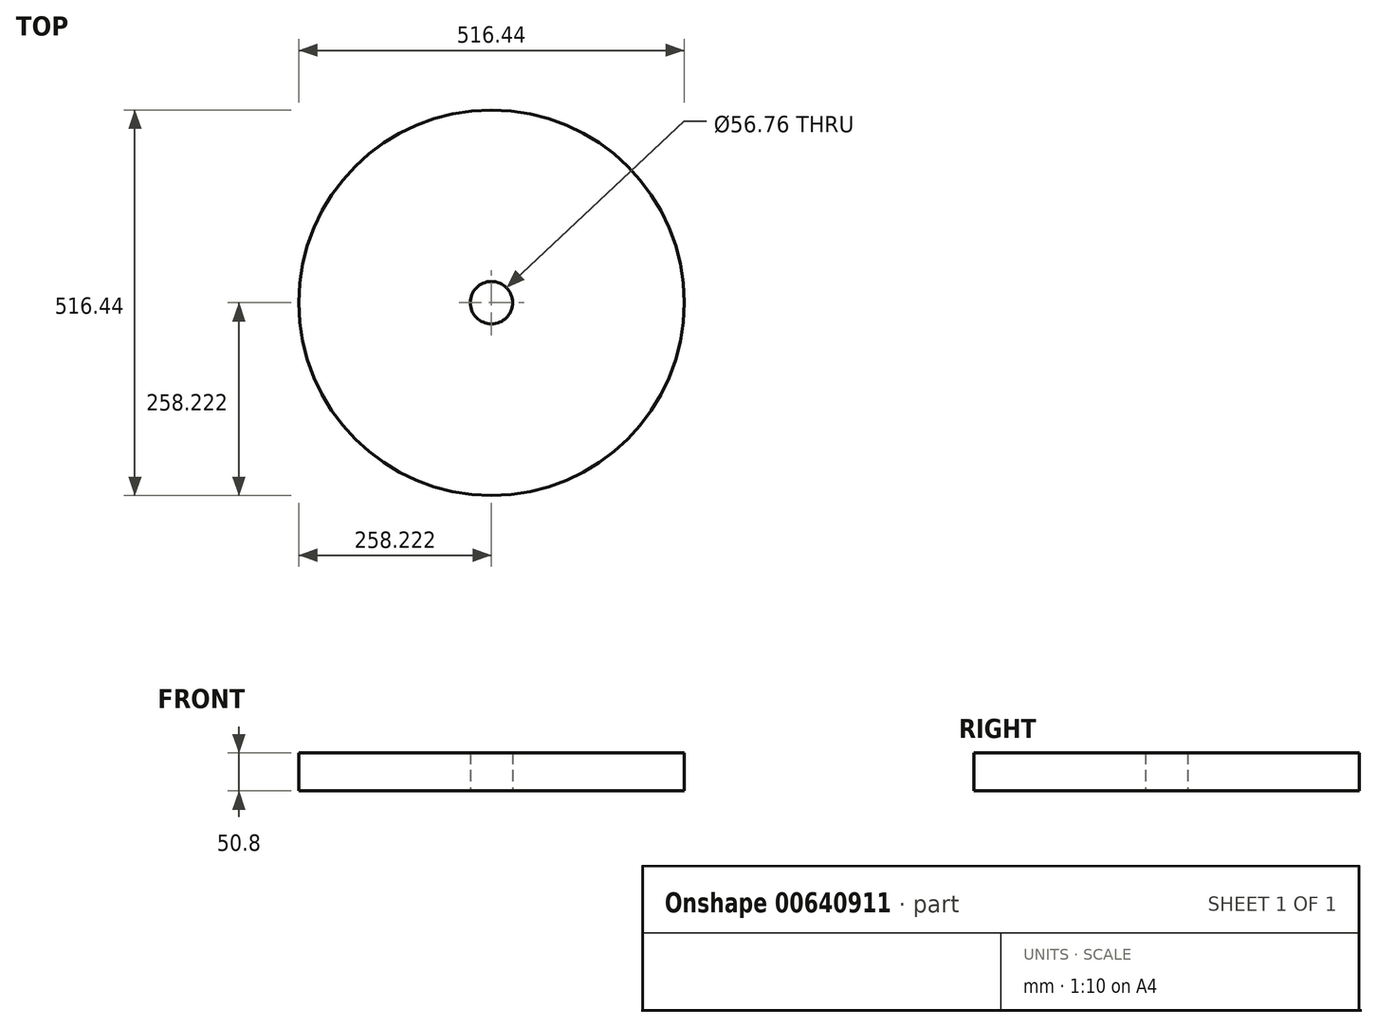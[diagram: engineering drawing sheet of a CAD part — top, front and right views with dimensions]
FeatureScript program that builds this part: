
annotation { "Feature Type Name" : "Feature", "Feature Type Description" : "" }
export const myFeature = defineFeature(function(context is Context, id is Id, definition is map)
    precondition{}
    {
        {
            var Q0;
            Q0=qCreatedBy(makeId("Top.planeOp"),FACE);
            var sketch = newSketch(context, id + "F0", { "sketchPlane" : qUnion([Q0])});
            skCircle(sketch, "E0", {"center": v(17.1, 20.31) * mm, "radius": 28.38 * mm});
            skCircle(sketch, "E1", {"center": v(17.1, 20.31) * mm, "radius": 258.22 * mm});
            skSolve(sketch);
        }
        {
            var Q0;
            Q0=makeQuery(id+"F0.imprint","IMPRINT",FACE,{"disambiguationData":[TD([[makeQuery(id+"F0.imprint","IMPRINT",EDGE,{"derivedFrom":sQuery(id+"F0.wireOp",EDGE,"E0")}),-1.0]])]});
            extrude(context, id + "F1", {"entities" : qUnion([Q0]), "depth" : 50.8 * mm, "offsetDistance" : 25.4 * mm});
        }
    });
